# Revit family: kawneer-190-pr-ctr-01_16342
name_source: partatom
category: Doors
revit_build: Autodesk Revit 2015 (Build: 20140905_0730(x64)
units: mm (PartAtom-declared; Revit-internal decimal feet)

## types (2) — shared parameters
Assembly Code = B2030110
Description = The 190 Narrow Stile Entrance is enginResults in a slim look that meets virtually all construction requirements
eered for moderate traffic in applications such as stores, offices and apartment buildings. Vertical stile measures 2-1/8" (54); top rail 2-1/4" (57.2) and bottom rail 3-7/8" (98.4).
Door Frame = Kawneer - Fluropon_Bone White-391X035
Door Glazing = Glass
Door Panel = Kawneer - Fluropon_Bone White-391X035
Function = Interior
Height = 7' - 0"
Manufacturer = Kawneer
Opening Width = 6' - 0"
Product data url = https://bimobject.com
Rough Height = 7' - 2"
Rough Width = 3' - 4"
Thickness = 0' - 1 3/4"
Type Comments = CENTER HUNG
URL = http://www.kawneer.com
Wall Closure = By host
Width = 3' - 0"

## per-type parameters (varying)
| type | Bottom Rail Height | Model |
| (2)3' x 7' B.R. 3 7/8" | 0' - 3 7/8" | Pair 190 Narrow Stile Door Center Set B.R. 3 7/8" |
| (2)3' x 7' B.R. 7 1/2" | 0' - 7 1/2" | Pair 190 Narrow Stile Door Center Set B.R. 7 1/2" |

## geometry (parser evidence)
native form markers: Extrusion x1, Sweep x2
no freeform markers — native parametric forms only
